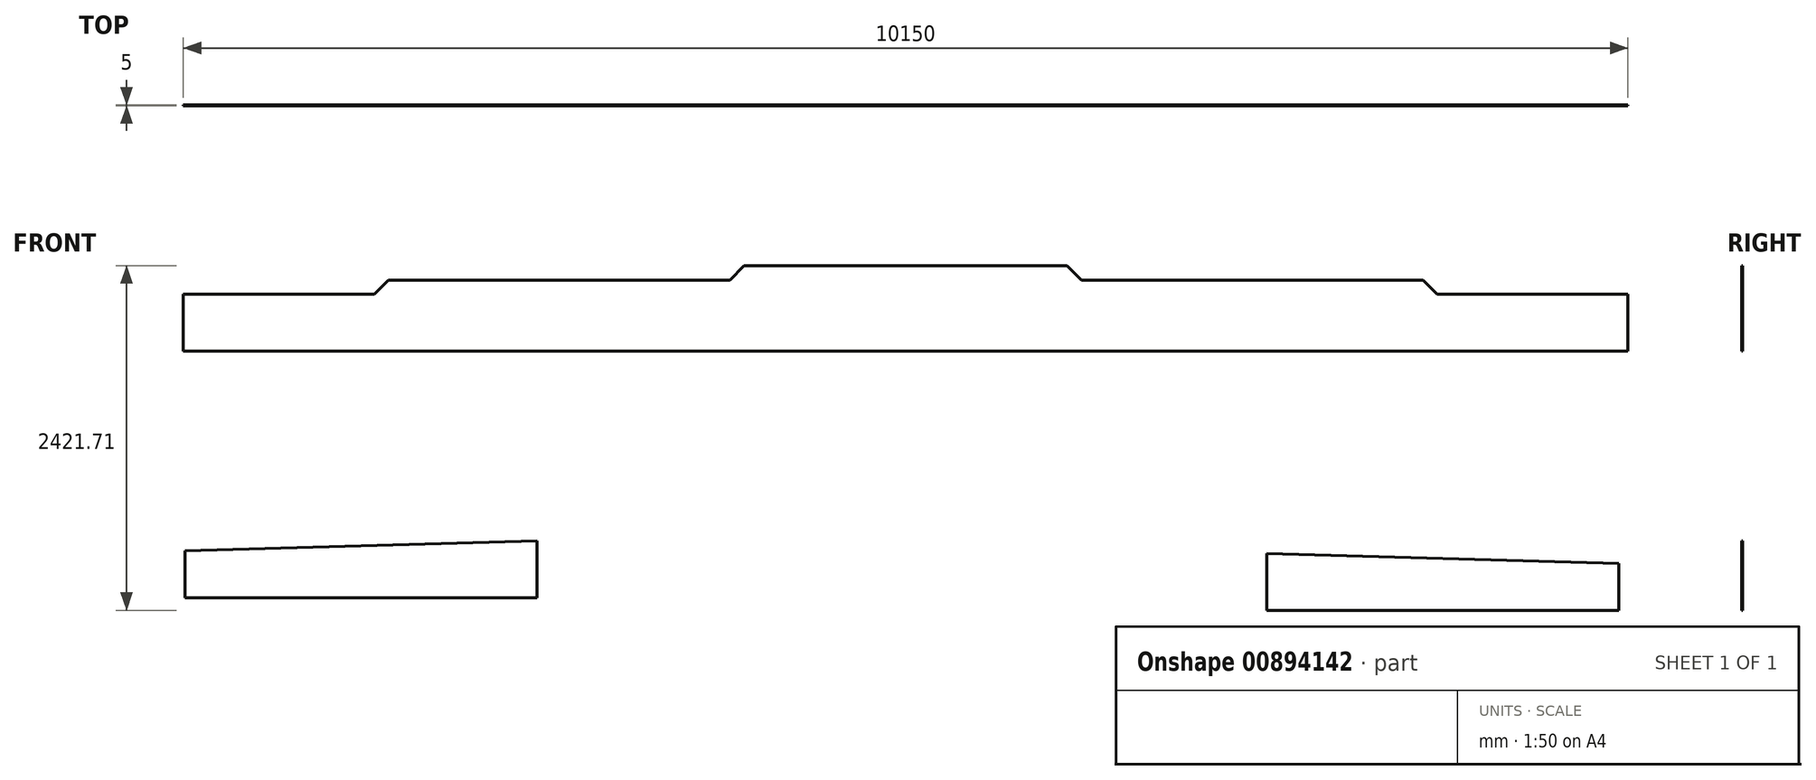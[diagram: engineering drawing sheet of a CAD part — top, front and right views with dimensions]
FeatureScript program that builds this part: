
annotation { "Feature Type Name" : "Feature", "Feature Type Description" : "" }
export const myFeature = defineFeature(function(context is Context, id is Id, definition is map)
    precondition{}
    {
        {
            var Q0;
            Q0=qCreatedBy(makeId("Front.planeOp"),FACE);
            var sketch = newSketch(context, id + "F0", { "sketchPlane" : qUnion([Q0])});
            skLineSegment(sketch, "E0", {"start": v(0, 0) * mm, "end": v(5075, 0) * mm});
            skLineSegment(sketch, "E1", {"start": v(-5075, 0) * mm, "end": v(0, 0) * mm});
            skLineSegment(sketch, "E2", {"start": v(-5075, 0) * mm, "end": v(-5075, 400) * mm});
            skLineSegment(sketch, "E3", {"start": v(5075, 0) * mm, "end": v(5075, 400) * mm});
            skLineSegment(sketch, "E4", {"start": v(-5075, 400) * mm, "end": v(-3735, 400) * mm});
            skLineSegment(sketch, "E5", {"start": v(-3735, 400) * mm, "end": v(-3635, 500) * mm});
            skLineSegment(sketch, "E6", {"start": v(-3635, 500) * mm, "end": v(-1235, 500) * mm});
            skLineSegment(sketch, "E7", {"start": v(-1235, 500) * mm, "end": v(-1135, 600) * mm});
            skLineSegment(sketch, "E8", {"start": v(-1135, 600) * mm, "end": v(0, 600) * mm});
            skLineSegment(sketch, "E9", {"start": v(5075, 400) * mm, "end": v(3735, 400) * mm});
            skLineSegment(sketch, "E10", {"start": v(3735, 400) * mm, "end": v(3635, 500) * mm});
            skLineSegment(sketch, "E11", {"start": v(3635, 500) * mm, "end": v(1235, 500) * mm});
            skLineSegment(sketch, "E12", {"start": v(1235, 500) * mm, "end": v(1135, 600) * mm});
            skLineSegment(sketch, "E13", {"start": v(1135, 600) * mm, "end": v(0, 600) * mm});
            skLineSegment(sketch, "E14", {"start": v(2536.41, -1821.71) * mm, "end": v(5011.41, -1821.71) * mm});
            skLineSegment(sketch, "E15", {"start": v(5011.41, -1821.71) * mm, "end": v(5011.41, -1491.71) * mm});
            skLineSegment(sketch, "E16", {"start": v(5011.41, -1491.71) * mm, "end": v(2536.41, -1421.71) * mm});
            skLineSegment(sketch, "E17", {"start": v(2536.41, -1421.71) * mm, "end": v(2536.41, -1821.71) * mm});
            skLineSegment(sketch, "E18", {"start": v(-5065.04, -1402.53) * mm, "end": v(-5065.04, -1732.53) * mm});
            skLineSegment(sketch, "E19", {"start": v(-5065.04, -1732.53) * mm, "end": v(-2590.04, -1732.53) * mm});
            skLineSegment(sketch, "E20", {"start": v(-2590.04, -1732.53) * mm, "end": v(-2590.04, -1332.53) * mm});
            skLineSegment(sketch, "E21", {"start": v(-2590.04, -1332.53) * mm, "end": v(-5065.04, -1402.53) * mm});
            skSolve(sketch);
        }
        {
            var Q0;
            Q0=makeQuery(id+"F0.imprint","IMPRINT",FACE,{"disambiguationData":[TD([[makeQuery(id+"F0.imprint","IMPRINT",EDGE,{"derivedFrom":sQuery(id+"F0.wireOp",EDGE,"E0")}),1.0]])]});
            var Q1;
            Q1=makeQuery(id+"F0.imprint","IMPRINT",FACE,{"disambiguationData":[TD([[makeQuery(id+"F0.imprint","IMPRINT",EDGE,{"derivedFrom":sQuery(id+"F0.wireOp",EDGE,"E18")}),1.0]])]});
            var Q2;
            Q2=makeQuery(id+"F0.imprint","IMPRINT",FACE,{"disambiguationData":[TD([[makeQuery(id+"F0.imprint","IMPRINT",EDGE,{"derivedFrom":sQuery(id+"F0.wireOp",EDGE,"E14")}),1.0]])]});
            extrude(context, id + "F1", {"entities" : qUnion([Q0, Q1, Q2]), "depth" : 5 * mm, "offsetDistance" : 25 * mm});
        }
    });
